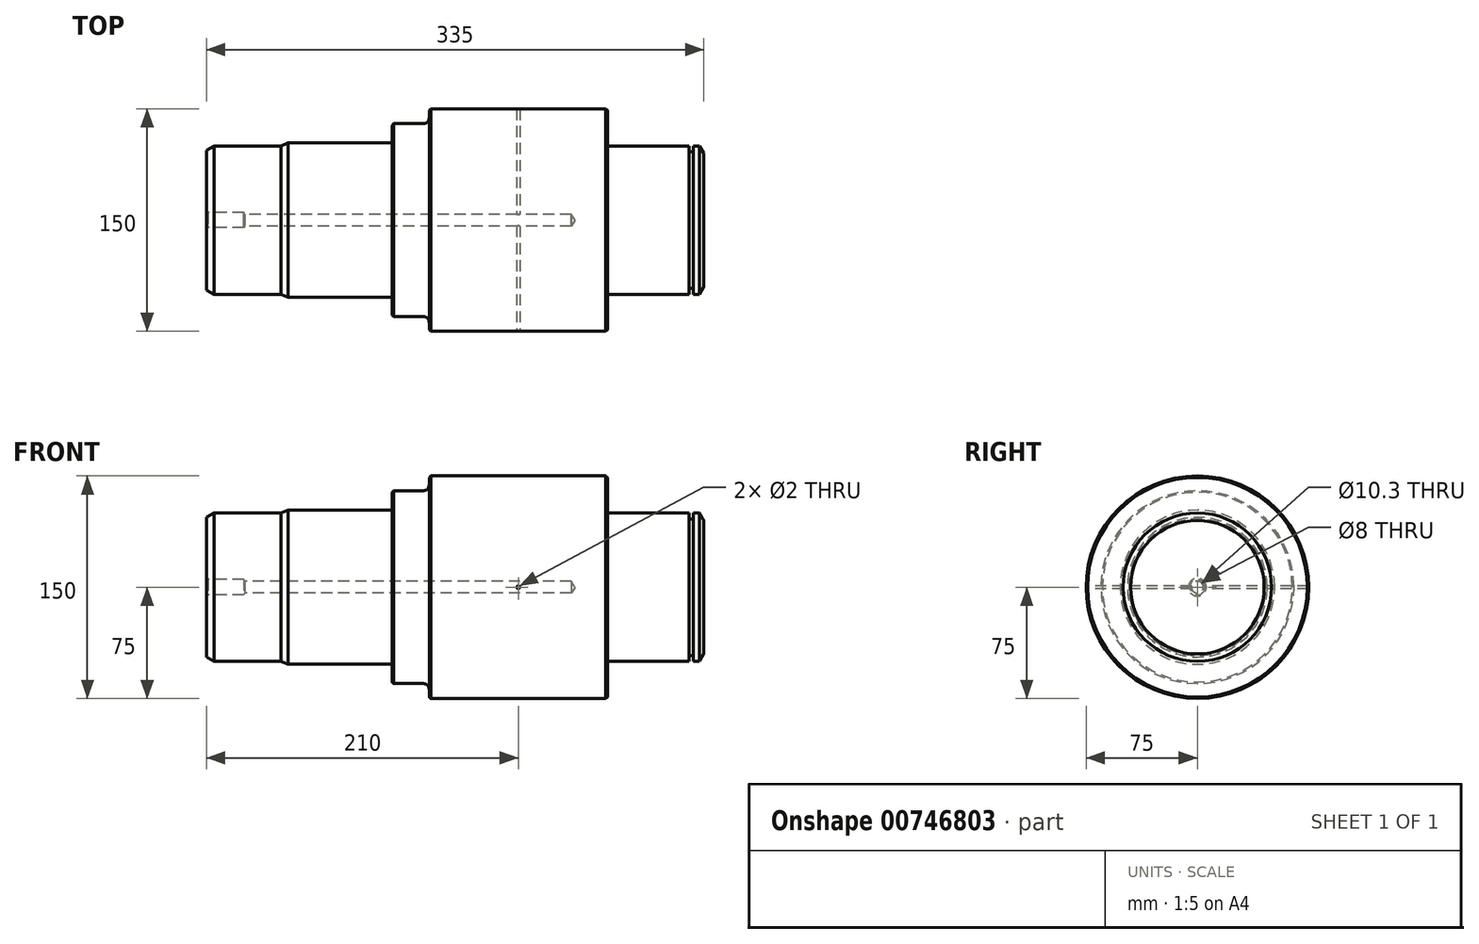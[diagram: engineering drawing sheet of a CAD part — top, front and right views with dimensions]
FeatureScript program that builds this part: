
annotation { "Feature Type Name" : "Feature", "Feature Type Description" : "" }
export const myFeature = defineFeature(function(context is Context, id is Id, definition is map)
    precondition{}
    {
        {
            var Q0;
            Q0=qCreatedBy(makeId("Front.planeOp"),FACE);
            var sketch = newSketch(context, id + "F0", { "sketchPlane" : qUnion([Q0])});
            skLineSegment(sketch, "E0", {"start": v(0, 0) * mm, "end": v(-250, 0) * mm});
            skLineSegment(sketch, "E1", {"start": v(-250, 0) * mm, "end": v(-250, 50) * mm});
            skLineSegment(sketch, "E2", {"start": v(-250, 50) * mm, "end": v(-200, 50) * mm});
            skLineSegment(sketch, "E3", {"start": v(-200, 50) * mm, "end": v(-195, 52) * mm});
            skLineSegment(sketch, "E4", {"start": v(-195, 52) * mm, "end": v(-125, 52) * mm});
            skLineSegment(sketch, "E5", {"start": v(-125, 52) * mm, "end": v(-125, 65) * mm});
            skLineSegment(sketch, "E6", {"start": v(-125, 65) * mm, "end": v(-100, 65) * mm});
            skLineSegment(sketch, "E7", {"start": v(-100, 65) * mm, "end": v(-100, 75) * mm});
            skLineSegment(sketch, "E8", {"start": v(-100, 75) * mm, "end": v(20, 75) * mm});
            skLineSegment(sketch, "E9", {"start": v(20, 75) * mm, "end": v(20, 50) * mm});
            skLineSegment(sketch, "E10", {"start": v(20, 50) * mm, "end": v(75, 50) * mm});
            skLineSegment(sketch, "E11", {"start": v(75, 50) * mm, "end": v(75, 46) * mm});
            skLineSegment(sketch, "E12", {"start": v(75, 46) * mm, "end": v(78, 46) * mm});
            skLineSegment(sketch, "E13", {"start": v(78, 46) * mm, "end": v(78, 50) * mm});
            skLineSegment(sketch, "E14", {"start": v(78, 50) * mm, "end": v(85, 50) * mm});
            skLineSegment(sketch, "E15", {"start": v(85, 50) * mm, "end": v(85, 0) * mm});
            skLineSegment(sketch, "E16", {"start": v(85, 0) * mm, "end": v(0, 0) * mm});
            skSolve(sketch);
        }
        {
            var Q0;
            Q0 = qSketchRegion(id + "F0", true);
            var Q1;
            Q1=sQuery(id+"F0.wireOp",EDGE,"E0");
            revolve(context, id + "F1", {"surfaceOperationType" : NewSurfaceOperationType.NEW, "entities" : qUnion([Q0]), "axis" : qUnion([Q1]), "revolveType" : RevolveType.FULL});
        }
        {
            var Q0;
            Q0=makeQuery(id+"F1.opRevolve","SWEPT_EDGE",EDGE,{"disambiguationData":[OSD([sQuery(id+"F0.wireOp",EDGE,"E14"),sQuery(id+"F0.wireOp",EDGE,"E15")])]});
            var Q1;
            Q1=makeQuery(id+"F1.opRevolve","SWEPT_EDGE",EDGE,{"disambiguationData":[OSD([sQuery(id+"F0.wireOp",EDGE,"E1"),sQuery(id+"F0.wireOp",EDGE,"E2")])]});
            chamfer(context, id + "F2", {"entities" : qUnion([Q0, Q1]), "chamferType" : ChamferType.OFFSET_ANGLE, "width" : 5 * mm, "oppositeDirection" : false, "angle" : 30 * degree, "tangentPropagation" : true});
        }
        {
            var Q0;
            Q0=makeQuery(id+"F1.opRevolve","SWEPT_EDGE",EDGE,{"disambiguationData":[OSD([sQuery(id+"F0.wireOp",EDGE,"E7"),sQuery(id+"F0.wireOp",EDGE,"E8")])]});
            var Q1;
            Q1=makeQuery(id+"F1.opRevolve","SWEPT_EDGE",EDGE,{"disambiguationData":[OSD([sQuery(id+"F0.wireOp",EDGE,"E5"),sQuery(id+"F0.wireOp",EDGE,"E6")])]});
            var Q2;
            Q2=makeQuery(id+"F1.opRevolve","SWEPT_EDGE",EDGE,{"disambiguationData":[OSD([sQuery(id+"F0.wireOp",EDGE,"E8"),sQuery(id+"F0.wireOp",EDGE,"E9")])]});
            chamfer(context, id + "F3", {"entities" : qUnion([Q0, Q1, Q2]), "width" : 1 * mm, "tangentPropagation" : true});
        }
        {
            var Q0;
            Q0=makeQuery(id+"F1.opRevolve","SWEPT_EDGE",EDGE,{"disambiguationData":[OSD([sQuery(id+"F0.wireOp",EDGE,"E4"),sQuery(id+"F0.wireOp",EDGE,"E5")])]});
            var Q1;
            Q1=makeQuery(id+"F1.opRevolve","SWEPT_EDGE",EDGE,{"disambiguationData":[OSD([sQuery(id+"F0.wireOp",EDGE,"E9"),sQuery(id+"F0.wireOp",EDGE,"E10")])]});
            fillet(context, id + "F4", {"entities" : qUnion([Q0, Q1]), "radius" : 1 * mm, "tangentPropagation" : true, "allowEdgeOverflow" : false});
        }
        {
            var Q0;
            Q0=makeQuery(id+"F1.opRevolve","SWEPT_EDGE",EDGE,{"disambiguationData":[OSD([sQuery(id+"F0.wireOp",EDGE,"E6"),sQuery(id+"F0.wireOp",EDGE,"E7")])]});
            fillet(context, id + "F5", {"entities" : qUnion([Q0]), "radius" : 4 * mm, "tangentPropagation" : true, "allowEdgeOverflow" : false});
        }
        {
            var Q0;
            Q0=makeQuery(id+"F1.opRevolve","SWEPT_FACE",FACE,{"disambiguationData":[OSD([sQuery(id+"F0.wireOp",EDGE,"E1")])]});
            var sketch = newSketch(context, id + "F6", { "sketchPlane" : qUnion([Q0])});
            skPoint(sketch, "E17", {"position": v(0, 0) * mm});
            skSolve(sketch);
        }
        {
            var Q0;
            Q0=sQuery(id+"F6.wireOp",VERTEX,"E17");
            var Q1;
            Q1=makeQuery(id+"F1.opRevolve","SWEPT_BODY",BODY,{"disambiguationData":[OSD([sQuery(id+"F0.wireOp",EDGE,"E0"),sQuery(id+"F0.wireOp",EDGE,"E1"),sQuery(id+"F0.wireOp",EDGE,"E2"),sQuery(id+"F0.wireOp",EDGE,"E3"),sQuery(id+"F0.wireOp",EDGE,"E4"),sQuery(id+"F0.wireOp",EDGE,"E5"),sQuery(id+"F0.wireOp",EDGE,"E6"),sQuery(id+"F0.wireOp",EDGE,"E7"),sQuery(id+"F0.wireOp",EDGE,"E8"),sQuery(id+"F0.wireOp",EDGE,"E9"),sQuery(id+"F0.wireOp",EDGE,"E10"),sQuery(id+"F0.wireOp",EDGE,"E11"),sQuery(id+"F0.wireOp",EDGE,"E12"),sQuery(id+"F0.wireOp",EDGE,"E13"),sQuery(id+"F0.wireOp",EDGE,"E14"),sQuery(id+"F0.wireOp",EDGE,"E15"),sQuery(id+"F0.wireOp",EDGE,"E16")])]});
            hole(context, id + "F7", {"style" : HoleStyle.C_SINK, "endStyle" : HoleEndStyle.BLIND, "holeDiameter" : 10.3 * mm, "cSinkDiameter" : 12 * mm, "cSinkAngle" : 90 * degree, "majorDiameter" : 12 * mm, "holeDepth" : 25 * mm, "isTappedThrough" : true, "tappedDepth" : 12 * mm, "tapClearance" : 3, "locations" : qUnion([Q0]), "scope" : qUnion([Q1])});
        }
        {
            var Q0;
            Q0=qCreatedBy(makeId("Front.planeOp"),FACE);
            var sketch = newSketch(context, id + "F8", { "sketchPlane" : qUnion([Q0])});
            skLineSegment(sketch, "E18", {"start": v(20, 0) * mm, "end": v(-100, 0) * mm, "construction": true});
            skSolve(sketch);
        }
        {
            var Q0;
            Q0=qCreatedBy(makeId("Front.planeOp"),FACE);
            cPlane(context, id + "F9", {"entities" : qUnion([Q0]), "cplaneType" : CPlaneType.OFFSET, "offset" : 75 * mm, "width" : 150 * mm, "height" : 150 * mm});
        }
        {
            var Q0;
            Q0=qCreatedBy(id+"F9.planeOp",FACE);
            var sketch = newSketch(context, id + "F10", { "sketchPlane" : qUnion([Q0])});
            skLineSegment(sketch, "E19.0", {"start": v(20, 0) * mm, "end": v(-100, 0) * mm, "construction": true});
            skPoint(sketch, "E20", {"position": v(-40, 0) * mm});
            skSolve(sketch);
        }
        {
            var Q0;
            Q0=sQuery(id+"F10.wireOp",VERTEX,"E20");
            var Q1;
            Q1=makeQuery(id+"F1.opRevolve","SWEPT_BODY",BODY,{"disambiguationData":[OSD([sQuery(id+"F0.wireOp",EDGE,"E0"),sQuery(id+"F0.wireOp",EDGE,"E1"),sQuery(id+"F0.wireOp",EDGE,"E2"),sQuery(id+"F0.wireOp",EDGE,"E3"),sQuery(id+"F0.wireOp",EDGE,"E4"),sQuery(id+"F0.wireOp",EDGE,"E5"),sQuery(id+"F0.wireOp",EDGE,"E6"),sQuery(id+"F0.wireOp",EDGE,"E7"),sQuery(id+"F0.wireOp",EDGE,"E8"),sQuery(id+"F0.wireOp",EDGE,"E9"),sQuery(id+"F0.wireOp",EDGE,"E10"),sQuery(id+"F0.wireOp",EDGE,"E11"),sQuery(id+"F0.wireOp",EDGE,"E12"),sQuery(id+"F0.wireOp",EDGE,"E13"),sQuery(id+"F0.wireOp",EDGE,"E14"),sQuery(id+"F0.wireOp",EDGE,"E15"),sQuery(id+"F0.wireOp",EDGE,"E16")])]});
            hole(context, id + "F11", {"style" : HoleStyle.SIMPLE, "endStyle" : HoleEndStyle.THROUGH, "holeDiameter" : 2 * mm, "majorDiameter" : 5 * mm, "isTappedThrough" : true, "tappedDepth" : 12 * mm, "tapClearance" : 3, "locations" : qUnion([Q0]), "scope" : qUnion([Q1])});
        }
        {
            var Q0;
            Q0=sQuery(id+"F6.wireOp",VERTEX,"E17");
            var Q1;
            Q1=makeQuery(id+"F1.opRevolve","SWEPT_BODY",BODY,{"disambiguationData":[OSD([sQuery(id+"F0.wireOp",EDGE,"E0"),sQuery(id+"F0.wireOp",EDGE,"E1"),sQuery(id+"F0.wireOp",EDGE,"E2"),sQuery(id+"F0.wireOp",EDGE,"E3"),sQuery(id+"F0.wireOp",EDGE,"E4"),sQuery(id+"F0.wireOp",EDGE,"E5"),sQuery(id+"F0.wireOp",EDGE,"E6"),sQuery(id+"F0.wireOp",EDGE,"E7"),sQuery(id+"F0.wireOp",EDGE,"E8"),sQuery(id+"F0.wireOp",EDGE,"E9"),sQuery(id+"F0.wireOp",EDGE,"E10"),sQuery(id+"F0.wireOp",EDGE,"E11"),sQuery(id+"F0.wireOp",EDGE,"E12"),sQuery(id+"F0.wireOp",EDGE,"E13"),sQuery(id+"F0.wireOp",EDGE,"E14"),sQuery(id+"F0.wireOp",EDGE,"E15"),sQuery(id+"F0.wireOp",EDGE,"E16")])]});
            hole(context, id + "F12", {"style" : HoleStyle.SIMPLE, "endStyle" : HoleEndStyle.BLIND, "holeDiameter" : 8 * mm, "majorDiameter" : 5 * mm, "holeDepth" : 220 * mm, "isTappedThrough" : true, "tappedDepth" : 12 * mm, "tapClearance" : 3, "locations" : qUnion([Q0]), "scope" : qUnion([Q1])});
        }
    });
